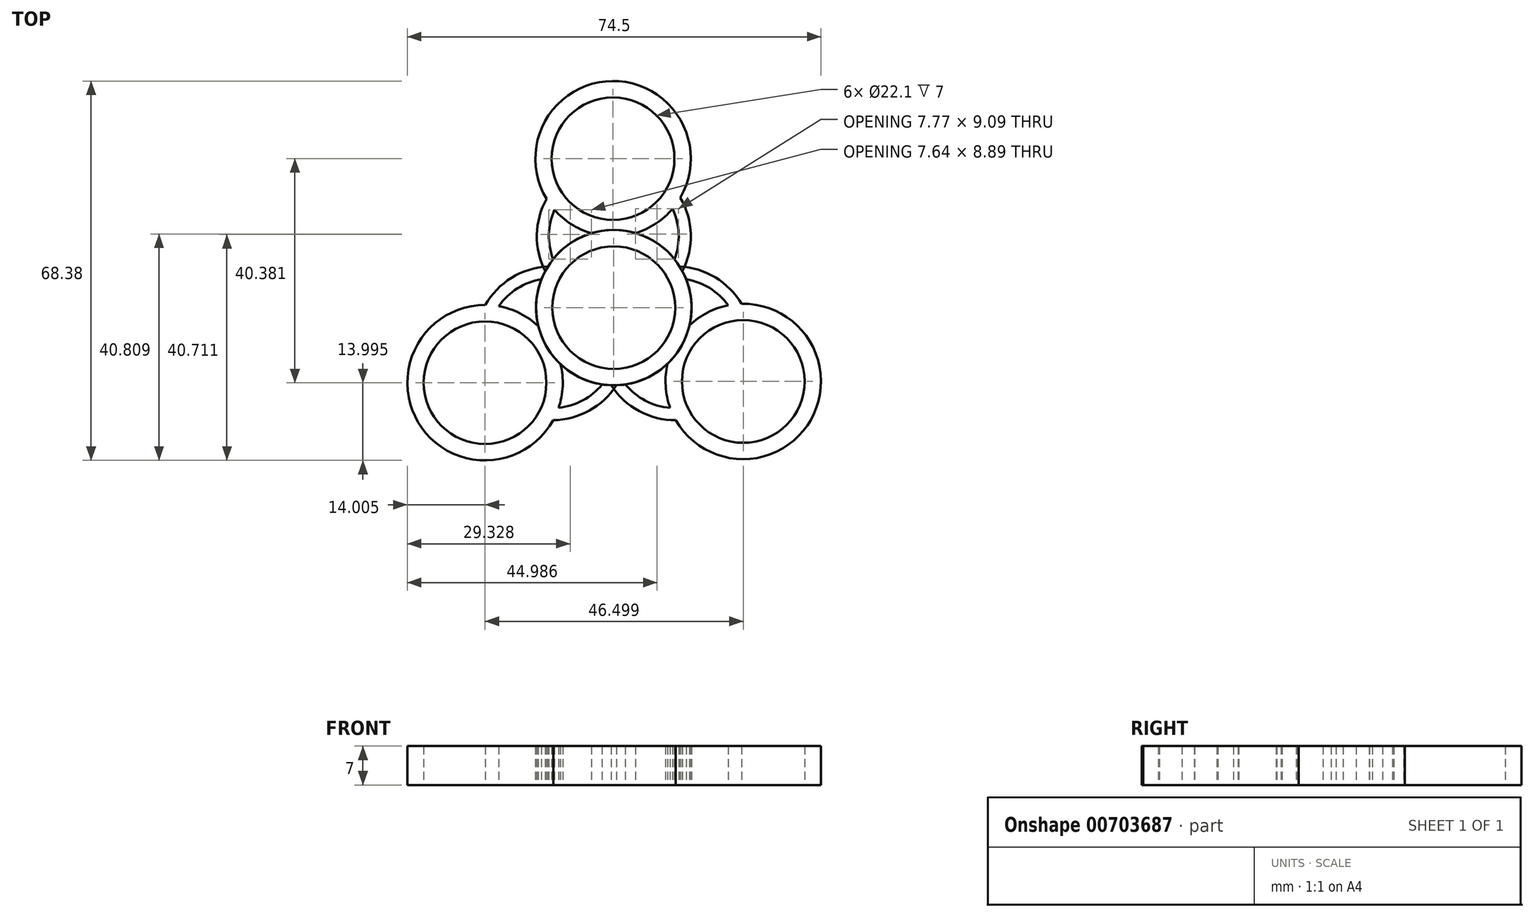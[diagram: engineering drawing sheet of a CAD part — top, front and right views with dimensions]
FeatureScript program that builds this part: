
annotation { "Feature Type Name" : "Feature", "Feature Type Description" : "" }
export const myFeature = defineFeature(function(context is Context, id is Id, definition is map)
    precondition{}
    {
        {
            var Q0;
            Q0=qCreatedBy(makeId("Top.planeOp"),FACE);
            var sketch = newSketch(context, id + "F0", { "sketchPlane" : qUnion([Q0])});
            skLineSegment(sketch, "E0.top", {"start": v(13.87, 26.85) * mm, "end": v(-14.13, 26.85) * mm});
            skPoint(sketch, "E0.middle", {"position": v(0, 0) * mm});
            skCircle(sketch, "E1", {"center": v(-0.13, 26.85) * mm, "radius": 14 * mm});
            skCircle(sketch, "E2", {"center": v(-0.13, 26.85) * mm, "radius": 11.05 * mm});
            skCircle(sketch, "E3", {"center": v(0, 0) * mm, "radius": 14 * mm});
            skCircle(sketch, "E4", {"center": v(0, 0) * mm, "radius": 11.05 * mm});
            skCircle(sketch, "E5", {"center": v(0, 12.85) * mm, "radius": 13.86 * mm});
            skCircle(sketch, "E6", {"center": v(0, 12.85) * mm, "radius": 11.69 * mm});
            skSolve(sketch);
        }
        {
            var Q0;
            Q0=qSketchRegion(id+"F0",true);
            var Q1;
            {var subQ1=sQuery(id+"F0.wireOp",EDGE,"E1");var subQ4=sQuery(id+"F0.wireOp",EDGE,"E6");var subQ9=makeQuery(id+"F0.imprint","INTERSECT",VERTEX,{"disambiguationData":[OD(0.0)],"derivedFrom":[subQ1,subQ4]});Q1=makeQuery(id+"F0.imprint","IMPRINT",FACE,{"disambiguationData":[TD([[makeQuery(id+"F0.imprint","IMPRINT",EDGE,{"disambiguationData":[TD([[subQ9,-1.0]])],"derivedFrom":subQ1}),1.0]])]});}
            var Q2;
            {var subQ4=sQuery(id+"F0.wireOp",EDGE,"E3");var subQ5=sQuery(id+"F0.wireOp",EDGE,"E1");var subQ6=makeQuery(id+"F0.imprint","INTERSECT",VERTEX,{"disambiguationData":[OD(0.0)],"derivedFrom":[subQ5,subQ4]});Q2=makeQuery(id+"F0.imprint","IMPRINT",FACE,{"disambiguationData":[TD([[makeQuery(id+"F0.imprint","IMPRINT",EDGE,{"disambiguationData":[TD([[subQ6,-1.0]])],"derivedFrom":subQ5}),-1.0]])]});}
            var Q3;
            {var subQ0=sQuery(id+"F0.wireOp",EDGE,"E3");var subQ1=sQuery(id+"F0.wireOp",EDGE,"E1");var subQ2=makeQuery(id+"F0.imprint","INTERSECT",VERTEX,{"disambiguationData":[OD(0.0)],"derivedFrom":[subQ1,subQ0]});Q3=makeQuery(id+"F0.imprint","IMPRINT",FACE,{"disambiguationData":[TD([[makeQuery(id+"F0.imprint","IMPRINT",EDGE,{"disambiguationData":[TD([[subQ2,-1.0]])],"derivedFrom":subQ1}),1.0]])]});}
            extrude(context, id + "F1", {"entities" : qUnion([Q0, Q1, Q2, Q3]), "depth" : 7 * mm, "offsetDistance" : 25 * mm});
        }
        {
            var Q0;
            Q0=qSketchRegion(id+"F0",true);
            extrude(context, id + "F2", {"entities" : qUnion([Q0]), "operationType" : NewBodyOperationType.ADD, "depth" : 7 * mm, "offsetDistance" : 25 * mm});
        }
        {
            var Q0;
            Q0=makeQuery(id+"F1.opExtrude","SWEPT_BODY",BODY,{"disambiguationData":[OSD([sQuery(id+"F0.wireOp",EDGE,"E1"),sQuery(id+"F0.wireOp",EDGE,"E2"),sQuery(id+"F0.wireOp",EDGE,"E3"),sQuery(id+"F0.wireOp",EDGE,"E4")])]});
            var Q1;
            Q1=sQuery(id+"F0.wireOp",EDGE,"E3");
            circularPattern(context, id + "F3", {"entities" : qUnion([Q0]), "axis" : qUnion([Q1]), "angle" : 360 * degree, "instanceCount" : 3, "equalSpace" : true});
        }
    });
